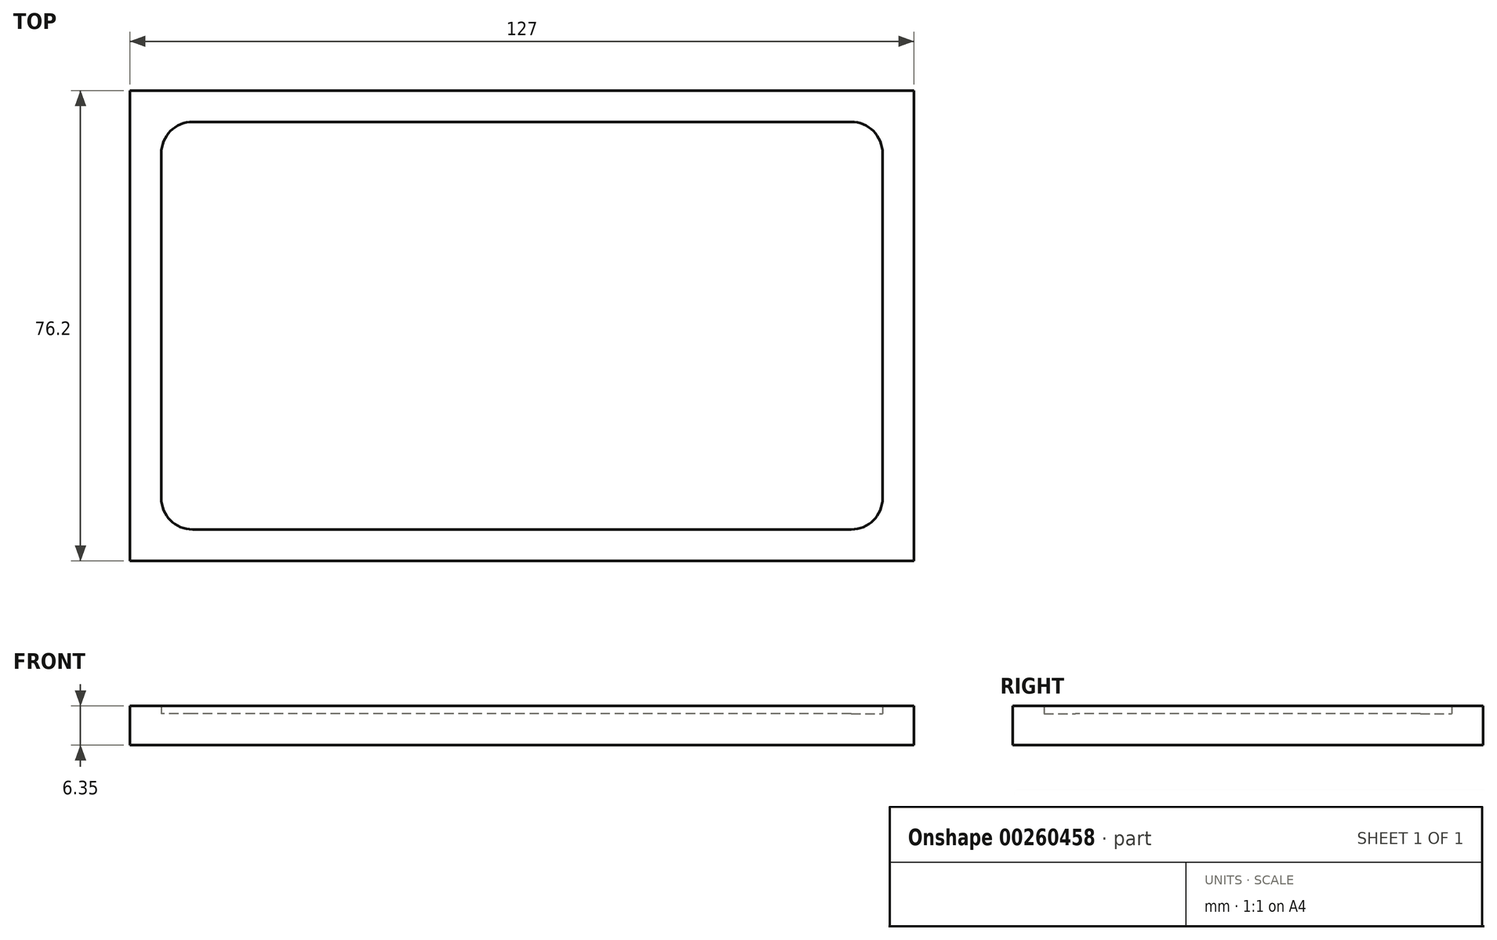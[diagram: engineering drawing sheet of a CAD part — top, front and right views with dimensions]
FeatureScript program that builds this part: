
annotation { "Feature Type Name" : "Feature", "Feature Type Description" : "" }
export const myFeature = defineFeature(function(context is Context, id is Id, definition is map)
    precondition{}
    {
        {
            var Q0;
            Q0=qCreatedBy(makeId("Top.planeOp"),FACE);
            var sketch = newSketch(context, id + "F0", { "sketchPlane" : qUnion([Q0])});
            skLineSegment(sketch, "E0.bottom", {"start": v(63.5, 38.1) * mm, "end": v(-63.5, 38.1) * mm});
            skLineSegment(sketch, "E0.top", {"start": v(63.5, -38.1) * mm, "end": v(-63.5, -38.1) * mm});
            skLineSegment(sketch, "E0.left", {"start": v(63.5, 38.1) * mm, "end": v(63.5, -38.1) * mm});
            skLineSegment(sketch, "E0.right", {"start": v(-63.5, 38.1) * mm, "end": v(-63.5, -38.1) * mm});
            skPoint(sketch, "E0.middle", {"position": v(0, 0) * mm});
            skSolve(sketch);
        }
        {
            var Q0;
            Q0 = qSketchRegion(id + "F0", true);
            extrude(context, id + "F1", {"entities" : qUnion([Q0]), "depth" : 6.35 * mm});
        }
        {
            var Q0;
            Q0=makeQuery(id+"F1.opExtrude","CAP_FACE",FACE,{"disambiguationData":[OSD([sQuery(id+"F0.wireOp",EDGE,"E0.bottom"),sQuery(id+"F0.wireOp",EDGE,"E0.top"),sQuery(id+"F0.wireOp",EDGE,"E0.left"),sQuery(id+"F0.wireOp",EDGE,"E0.right")])],"isStart":false});
            shell(context, id + "F2", {"entities" : qUnion([Q0]), "thickness" : 5.08 * mm});
        }
        {
            var Q0;
            Q0=makeQuery(id+"F2.opShell","OFFSET_EDGE",EDGE,{"disambiguationData":[OSD([sQuery(id+"F0.wireOp",EDGE,"E0.bottom"),sQuery(id+"F0.wireOp",EDGE,"E0.left")])]});
            fillet(context, id + "F3", {"entities" : qUnion([Q0]), "radius" : 5.08 * mm, "tangentPropagation" : true, "allowEdgeOverflow" : false});
        }
        {
            var Q0;
            Q0=makeQuery(id+"F2.opShell","OFFSET_EDGE",EDGE,{"disambiguationData":[OSD([sQuery(id+"F0.wireOp",EDGE,"E0.bottom"),sQuery(id+"F0.wireOp",EDGE,"E0.right")])]});
            fillet(context, id + "F4", {"entities" : qUnion([Q0]), "radius" : 5.08 * mm, "tangentPropagation" : true, "allowEdgeOverflow" : false});
        }
        {
            var Q0;
            Q0=makeQuery(id+"F2.opShell","OFFSET_EDGE",EDGE,{"disambiguationData":[OSD([sQuery(id+"F0.wireOp",EDGE,"E0.top"),sQuery(id+"F0.wireOp",EDGE,"E0.right")])]});
            fillet(context, id + "F5", {"entities" : qUnion([Q0]), "radius" : 5.08 * mm, "tangentPropagation" : true, "allowEdgeOverflow" : false});
        }
        {
            var Q0;
            Q0=makeQuery(id+"F2.opShell","OFFSET_EDGE",EDGE,{"disambiguationData":[OSD([sQuery(id+"F0.wireOp",EDGE,"E0.top"),sQuery(id+"F0.wireOp",EDGE,"E0.left")])]});
            fillet(context, id + "F6", {"entities" : qUnion([Q0]), "radius" : 5.08 * mm, "tangentPropagation" : true, "allowEdgeOverflow" : false});
        }
    });
